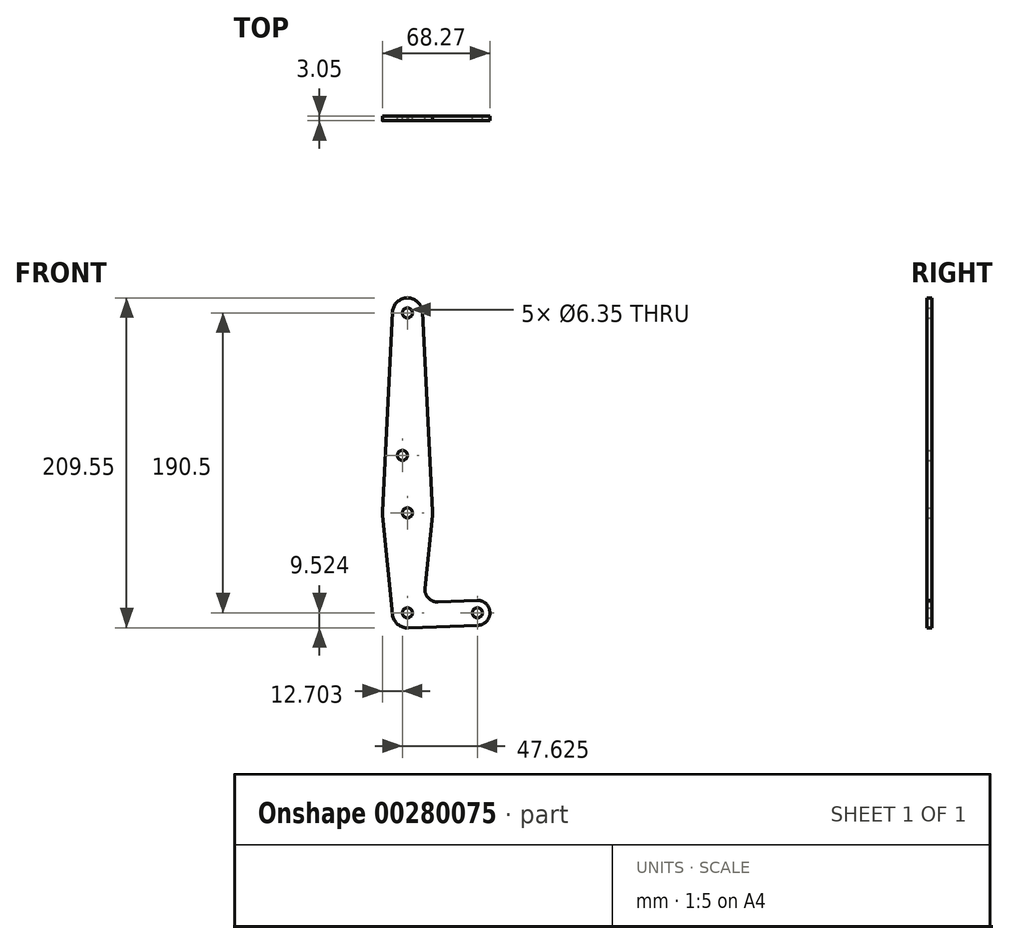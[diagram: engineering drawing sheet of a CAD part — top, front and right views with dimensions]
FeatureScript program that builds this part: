
annotation { "Feature Type Name" : "Feature", "Feature Type Description" : "" }
export const myFeature = defineFeature(function(context is Context, id is Id, definition is map)
    precondition{}
    {
        {
            var Q0;
            Q0=qCreatedBy(makeId("Front.planeOp"),FACE);
            var sketch = newSketch(context, id + "F0", { "sketchPlane" : qUnion([Q0])});
            skCircle(sketch, "E0", {"center": v(-6.78, 141.35) * mm, "radius": 9.53 * mm});
            skCircle(sketch, "E1", {"center": v(-6.78, 14.35) * mm, "radius": 15.88 * mm});
            skCircle(sketch, "E2", {"center": v(-6.78, -49.15) * mm, "radius": 9.53 * mm});
            skCircle(sketch, "E3", {"center": v(37.67, -49.15) * mm, "radius": 7.94 * mm});
            skLineSegment(sketch, "E4", {"start": v(-6.78, 141.35) * mm, "end": v(-6.78, -49.15) * mm, "construction": true});
            skLineSegment(sketch, "E5", {"start": v(-6.78, -49.15) * mm, "end": v(37.67, -49.15) * mm, "construction": true});
            skLineSegment(sketch, "E6", {"start": v(12.6, -42.25) * mm, "end": v(37.34, -41.22) * mm});
            skLineSegment(sketch, "E7", {"start": v(-6.78, -58.67) * mm, "end": v(37.95, -57.08) * mm});
            skLineSegment(sketch, "E8", {"start": v(-22.58, 12.77) * mm, "end": v(-16.26, -50.1) * mm});
            skLineSegment(sketch, "E9", {"start": v(9.01, 12.77) * mm, "end": v(4.36, -33.5) * mm});
            skCircle(sketch, "E10", {"center": v(-6.78, 141.35) * mm, "radius": 3.18 * mm});
            skCircle(sketch, "E11", {"center": v(-6.78, 14.35) * mm, "radius": 3.18 * mm});
            skCircle(sketch, "E12", {"center": v(-6.78, -49.15) * mm, "radius": 3.18 * mm});
            skCircle(sketch, "E13", {"center": v(37.67, -49.15) * mm, "radius": 3.18 * mm});
            skCircle(sketch, "E14", {"center": v(-9.96, 50.88) * mm, "radius": 3.18 * mm});
            skPoint(sketch, "E15.newPointA", {"position": v(0, -76.92) * mm});
            skArc(sketch, "E15.filletArc", {"start": v(4.36, -33.5) * mm, "mid": v(6.49, -39.76) * mm, "end": v(12.6, -42.25) * mm});
            skLineSegment(sketch, "E16", {"start": v(-16.3, 141.83) * mm, "end": v(-22.64, 15.15) * mm});
            skLineSegment(sketch, "E17", {"start": v(2.73, 141.83) * mm, "end": v(9.07, 15.15) * mm});
            skSolve(sketch);
        }
        {
            var Q0;
            Q0 = qSketchRegion(id + "F0", true);
            extrude(context, id + "F1", {"entities" : qUnion([Q0]), "depth" : 3.05 * mm});
        }
    });
